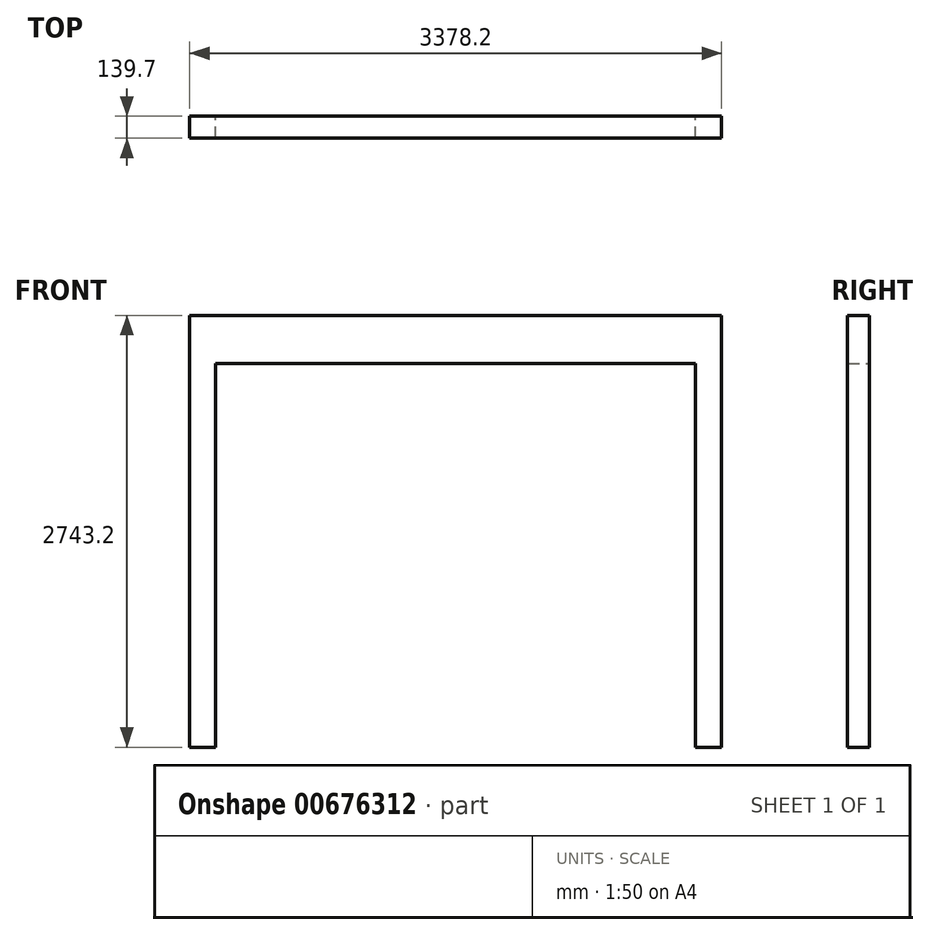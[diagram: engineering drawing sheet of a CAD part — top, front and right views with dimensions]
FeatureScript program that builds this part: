
annotation { "Feature Type Name" : "Feature", "Feature Type Description" : "" }
export const myFeature = defineFeature(function(context is Context, id is Id, definition is map)
    precondition{}
    {
        {
            var Q0;
            Q0=qCreatedBy(makeId("Front.planeOp"),FACE);
            var sketch = newSketch(context, id + "F0", { "sketchPlane" : qUnion([Q0])});
            skLineSegment(sketch, "E0.bottom", {"start": v(-1689.1, 0) * mm, "end": v(1689.1, 0) * mm, "construction": true});
            skLineSegment(sketch, "E0.top", {"start": v(-1689.1, 2743.2) * mm, "end": v(1689.1, 2743.2) * mm});
            skLineSegment(sketch, "E0.left", {"start": v(-1689.1, 0) * mm, "end": v(-1689.1, 2743.2) * mm});
            skLineSegment(sketch, "E0.right", {"start": v(1689.1, 0) * mm, "end": v(1689.1, 2743.2) * mm});
            skLineSegment(sketch, "E1", {"start": v(-1689.1, 0) * mm, "end": v(-1524, 0) * mm});
            skLineSegment(sketch, "E2", {"start": v(-1524, 0) * mm, "end": v(-1524, 2438.4) * mm});
            skLineSegment(sketch, "E3", {"start": v(-1524, 2438.4) * mm, "end": v(1524, 2438.4) * mm});
            skLineSegment(sketch, "E4", {"start": v(1524, 2438.4) * mm, "end": v(1524, 0) * mm});
            skLineSegment(sketch, "E5", {"start": v(1524, 0) * mm, "end": v(1689.1, 0) * mm});
            skSolve(sketch);
        }
        {
            var Q0;
            Q0 = qSketchRegion(id + "F0", true);
            extrude(context, id + "F1", {"entities" : qUnion([Q0]), "depth" : 139.7 * mm, "offsetDistance" : 25.4 * mm});
        }
    });
